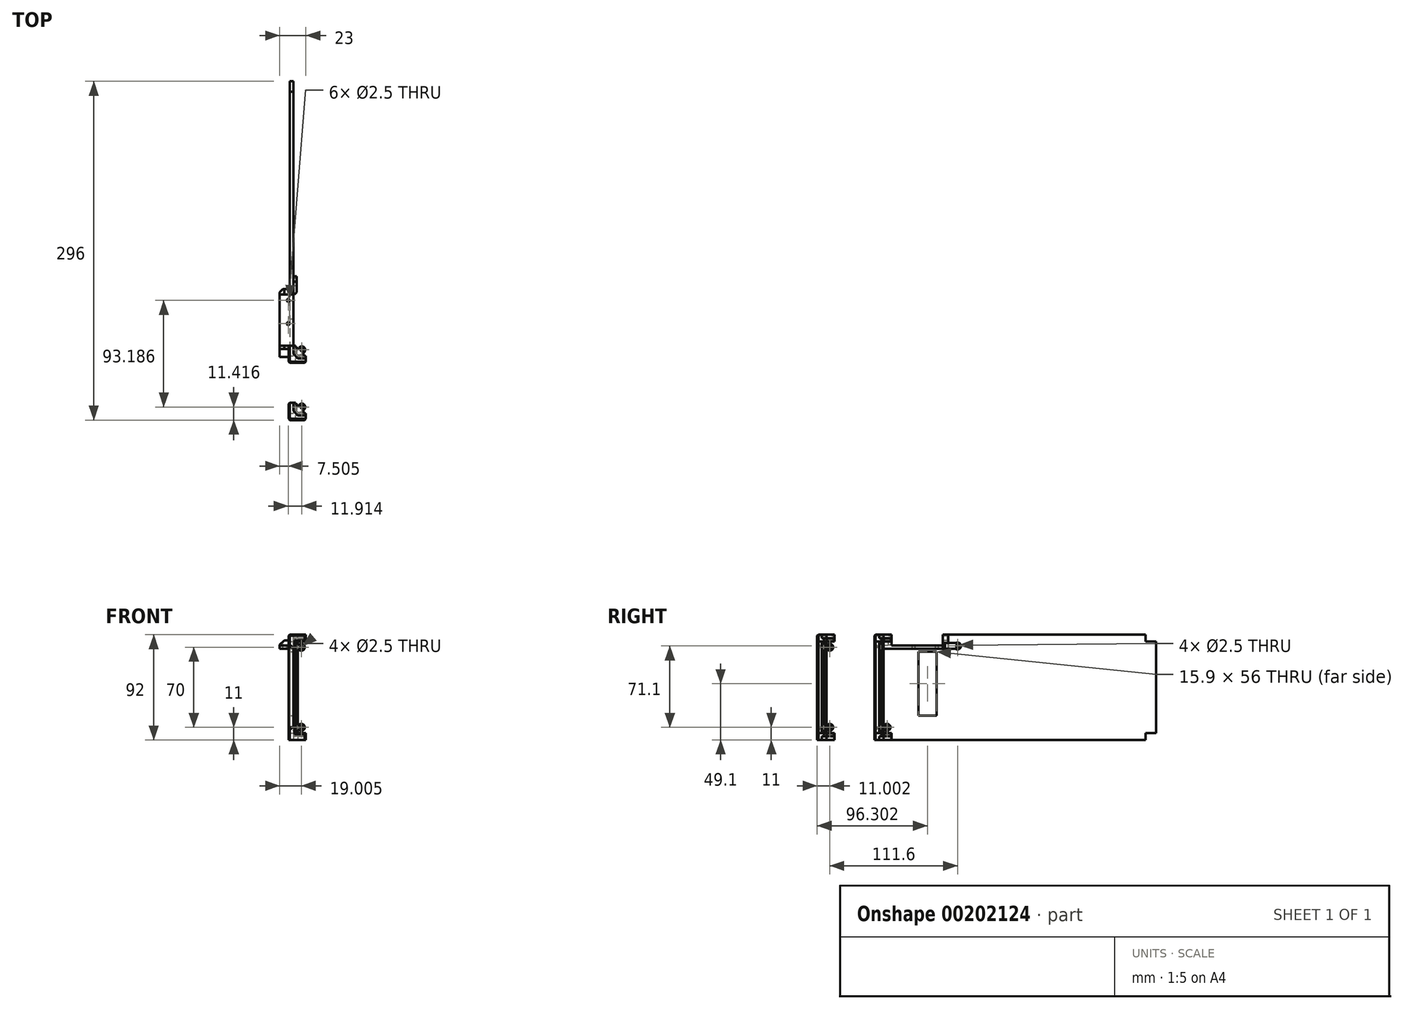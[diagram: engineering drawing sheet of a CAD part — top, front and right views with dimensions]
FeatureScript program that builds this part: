
annotation { "Feature Type Name" : "Feature", "Feature Type Description" : "" }
export const myFeature = defineFeature(function(context is Context, id is Id, definition is map)
    precondition{}
    {
        {
            var Q0;
            Q0=qCreatedBy(makeId("Top.planeOp"),FACE);
            var sketch = newSketch(context, id + "F0", { "sketchPlane" : qUnion([Q0])});
            skLineSegment(sketch, "E0", {"start": v(-30.7, 8.8) * mm, "end": v(-30.7, -6.2) * mm});
            skLineSegment(sketch, "E1", {"start": v(-30.7, -6.2) * mm, "end": v(-15.7, -6.2) * mm});
            skLineSegment(sketch, "E2", {"start": v(-30.7, 8.8) * mm, "end": v(-29.7, 8.8) * mm});
            skLineSegment(sketch, "E3", {"start": v(-15.7, -6.2) * mm, "end": v(-15.7, -5.2) * mm});
            skLineSegment(sketch, "E4", {"start": v(-29.7, 8.8) * mm, "end": v(-24.7, 8.8) * mm});
            skLineSegment(sketch, "E5", {"start": v(-15.7, -5.2) * mm, "end": v(-15.7, -0.2) * mm});
            skLineSegment(sketch, "E6", {"start": v(-24.7, 8.8) * mm, "end": v(-24.7, -0.2) * mm});
            skLineSegment(sketch, "E7", {"start": v(-24.7, -0.2) * mm, "end": v(-15.7, -0.2) * mm});
            skSolve(sketch);
        }
        {
            var Q0;
            Q0=makeQuery(id+"F0.imprint","IMPRINT",FACE,{"disambiguationData":[TD([[makeQuery(id+"F0.imprint","IMPRINT",EDGE,{"derivedFrom":sQuery(id+"F0.wireOp",EDGE,"E0")}),1.0]])]});
            extrude(context, id + "F1", {"entities" : qUnion([Q0]), "depth" : 6 * mm});
        }
        {
            var Q0;
            Q0=makeQuery(id+"F1.opExtrude","CAP_FACE",FACE,{"disambiguationData":[OSD([sQuery(id+"F0.wireOp",EDGE,"E0"),sQuery(id+"F0.wireOp",EDGE,"E1"),sQuery(id+"F0.wireOp",EDGE,"E2"),sQuery(id+"F0.wireOp",EDGE,"E3"),sQuery(id+"F0.wireOp",EDGE,"E4"),sQuery(id+"F0.wireOp",EDGE,"E5"),sQuery(id+"F0.wireOp",EDGE,"E6"),sQuery(id+"F0.wireOp",EDGE,"E7")])],"isStart":false});
            var sketch = newSketch(context, id + "F2", { "sketchPlane" : qUnion([Q0])});
            skLineSegment(sketch, "E8.top", {"start": v(-30.7, -0.2) * mm, "end": v(-24.7, -0.2) * mm});
            skLineSegment(sketch, "E9", {"start": v(-24.7, -0.2) * mm, "end": v(-24.7, 1.8) * mm});
            skLineSegment(sketch, "E10", {"start": v(-24.7, 1.8) * mm, "end": v(-26.7, 1.8) * mm});
            skLineSegment(sketch, "E11", {"start": v(-26.7, 1.8) * mm, "end": v(-26.7, -0.2) * mm});
            skLineSegment(sketch, "E12", {"start": v(-24.7, -0.2) * mm, "end": v(-22.7, -0.2) * mm});
            skLineSegment(sketch, "E13", {"start": v(-22.7, -0.2) * mm, "end": v(-22.7, -2.2) * mm});
            skLineSegment(sketch, "E14", {"start": v(-22.7, -2.2) * mm, "end": v(-24.7, -2.2) * mm});
            skLineSegment(sketch, "E15", {"start": v(-24.7, -6.2) * mm, "end": v(-29.7, -6.2) * mm});
            skLineSegment(sketch, "E16", {"start": v(-24.7, -6.2) * mm, "end": v(-24.7, -2.2) * mm});
            skLineSegment(sketch, "E17", {"start": v(-24.7, -0.2) * mm, "end": v(-24.7, -2.2) * mm});
            skLineSegment(sketch, "E18", {"start": v(-30.7, -0.2) * mm, "end": v(-30.7, -5.2) * mm});
            skLineSegment(sketch, "E19", {"start": v(-30.7, -5.2) * mm, "end": v(-29.7, -6.2) * mm});
            skSolve(sketch);
        }
        {
            var Q0;
            Q0=makeQuery(id+"F2.imprint","IMPRINT",FACE,{"disambiguationData":[TD([[makeQuery(id+"F2.imprint","IMPRINT",EDGE,{"derivedFrom":sQuery(id+"F2.wireOp",EDGE,"E8.bottom")}),1.0]])]});
            var Q1;
            {var subQ0=sQuery(id+"F2.wireOp",EDGE,"E12");Q1=makeQuery(id+"F2.imprint","IMPRINT",FACE,{"disambiguationData":[TD([[makeQuery(id+"F2.imprint","IMPRINT",EDGE,{"derivedFrom":subQ0}),-1.0]])]});}
            var Q2;
            Q2=makeQuery(id+"F2.imprint","IMPRINT",FACE,{"disambiguationData":[TD([[makeQuery(id+"F2.imprint","IMPRINT",EDGE,{"derivedFrom":sQuery(id+"F2.wireOp",EDGE,"E15")}),1.0]])]});
            var Q3;
            {var subQ0=sQuery(id+"F2.wireOp",EDGE,"E9");Q3=makeQuery(id+"F2.imprint","IMPRINT",FACE,{"disambiguationData":[TD([[makeQuery(id+"F2.imprint","IMPRINT",EDGE,{"derivedFrom":subQ0}),-1.0]])]});}
            extrude(context, id + "F3", {"entities" : qUnion([Q0, Q1, Q2, Q3]), "operationType" : NewBodyOperationType.ADD, "depth" : 5 * mm});
        }
        {
            var Q0;
            Q0=makeQuery(id+"F3.opExtrude","CAP_FACE",FACE,{"disambiguationData":[OSD([sQuery(id+"F2.wireOp",EDGE,"E8.bottom"),sQuery(id+"F2.wireOp",EDGE,"E8.top"),sQuery(id+"F2.wireOp",EDGE,"E8.left"),sQuery(id+"F2.wireOp",EDGE,"E8.right"),sQuery(id+"F2.wireOp",EDGE,"E9"),sQuery(id+"F2.wireOp",EDGE,"E10"),sQuery(id+"F2.wireOp",EDGE,"E11"),sQuery(id+"F2.wireOp",EDGE,"E12"),sQuery(id+"F2.wireOp",EDGE,"E13"),sQuery(id+"F2.wireOp",EDGE,"E14")])],"isStart":false});
            var sketch = newSketch(context, id + "F4", { "sketchPlane" : qUnion([Q0])});
            skLineSegment(sketch, "E20", {"start": v(-24.7, -6.2) * mm, "end": v(-26.7, -6.2) * mm});
            skLineSegment(sketch, "E21", {"start": v(-30.7, -0.2) * mm, "end": v(-30.7, -2.2) * mm});
            skLineSegment(sketch, "E22", {"start": v(-26.7, -6.2) * mm, "end": v(-30.7, -2.2) * mm});
            skLineSegment(sketch, "E23", {"start": v(-24.7, -6.2) * mm, "end": v(-24.7, -2.2) * mm});
            skLineSegment(sketch, "E24", {"start": v(-24.7, -2.2) * mm, "end": v(-22.7, -2.2) * mm});
            skLineSegment(sketch, "E25", {"start": v(-22.7, -2.2) * mm, "end": v(-22.7, -0.2) * mm});
            skLineSegment(sketch, "E26", {"start": v(-22.7, -0.2) * mm, "end": v(-24.7, -0.2) * mm});
            skLineSegment(sketch, "E27", {"start": v(-24.7, -0.2) * mm, "end": v(-24.7, 1.8) * mm});
            skLineSegment(sketch, "E28", {"start": v(-24.7, 1.8) * mm, "end": v(-26.7, 1.8) * mm});
            skLineSegment(sketch, "E29", {"start": v(-26.7, 1.8) * mm, "end": v(-26.7, -0.2) * mm});
            skLineSegment(sketch, "E30", {"start": v(-26.7, -0.2) * mm, "end": v(-30.7, -0.2) * mm});
            skSolve(sketch);
        }
        {
            var Q0;
            Q0=makeQuery(id+"F4.imprint","IMPRINT",FACE,{"disambiguationData":[TD([[makeQuery(id+"F4.imprint","IMPRINT",EDGE,{"derivedFrom":sQuery(id+"F4.wireOp",EDGE,"E20")}),1.0]])]});
            extrude(context, id + "F5", {"entities" : qUnion([Q0]), "operationType" : NewBodyOperationType.ADD, "depth" : 35 * mm});
        }
        {
            var Q0;
            Q0=makeQuery(id+"F5.boolean.opBoolean","MERGE",FACE,{"derivedFrom":[makeQuery(id+"F3.opExtrude","SWEPT_FACE",FACE,{"disambiguationData":[OSD([sQuery(id+"F2.wireOp",EDGE,"E14")])]}),makeQuery(id+"F5.opExtrude","SWEPT_FACE",FACE,{"disambiguationData":[OSD([sQuery(id+"FcikvxoAmVT8Sga_1.wireOp",EDGE,"Ugr4Xeua-PaRH-PEAE-46ir-bzMubUFrfAmX")])]})]});
            var sketch = newSketch(context, id + "F6", { "sketchPlane" : qUnion([Q0])});
            skLineSegment(sketch, "E31", {"start": v(-22.7, 6) * mm, "end": v(-22.7, 11) * mm});
            skLineSegment(sketch, "E32", {"start": v(-22.7, 11) * mm, "end": v(-19.7, 11) * mm});
            skCircle(sketch, "E33", {"center": v(-19.7, 11) * mm, "radius": 1.25 * mm});
            skCircle(sketch, "E34", {"center": v(-19.7, 11) * mm, "radius": 3 * mm});
            skLineSegment(sketch, "E35", {"start": v(-22.7, 6) * mm, "end": v(-22.7, 9) * mm});
            skLineSegment(sketch, "E36", {"start": v(-22.7, 9) * mm, "end": v(-21.94, 9) * mm});
            skLineSegment(sketch, "E37", {"start": v(-22.7, 11) * mm, "end": v(-22.7, 13) * mm});
            skLineSegment(sketch, "E38", {"start": v(-22.7, 13) * mm, "end": v(-21.94, 13) * mm});
            skSolve(sketch);
        }
        {
            var Q0;
            Q0=makeQuery(id+"F6.imprint","IMPRINT",FACE,{"disambiguationData":[TD([[makeQuery(id+"F6.imprint","IMPRINT",EDGE,{"derivedFrom":sQuery(id+"F6.wireOp",EDGE,"E33")}),-1.0]])]});
            var Q1;
            {var subQ0=sQuery(id+"F6.wireOp",EDGE,"E37");Q1=makeQuery(id+"F6.imprint","IMPRINT",FACE,{"disambiguationData":[TD([[makeQuery(id+"F6.imprint","IMPRINT",EDGE,{"derivedFrom":subQ0}),1.0]])]});}
            var Q2;
            {var subQ0=sQuery(id+"F6.wireOp",EDGE,"E31");Q2=makeQuery(id+"F6.imprint","IMPRINT",FACE,{"disambiguationData":[TD([[makeQuery(id+"F6.imprint","IMPRINT",EDGE,{"derivedFrom":subQ0}),1.0]])]});}
            extrude(context, id + "F7", {"entities" : qUnion([Q0, Q1, Q2]), "operationType" : NewBodyOperationType.ADD, "oppositeDirection" : true, "depth" : 3 * mm});
        }
        {
            var Q0;
            Q0=makeQuery(id+"F5.boolean.opBoolean","MERGE",FACE,{"derivedFrom":[makeQuery(id+"F3.opExtrude","SWEPT_FACE",FACE,{"disambiguationData":[OSD([sQuery(id+"F2.wireOp",EDGE,"E11")])]}),makeQuery(id+"F5.opExtrude","SWEPT_FACE",FACE,{"disambiguationData":[OSD([sQuery(id+"FcikvxoAmVT8Sga_1.wireOp",EDGE,"rjj8wiBv-6VFg-MGKm-luXr-hqUBBP5AjTz5")])]})]});
            var sketch = newSketch(context, id + "F8", { "sketchPlane" : qUnion([Q0])});
            skLineSegment(sketch, "E39", {"start": v(-1.8, 6) * mm, "end": v(-1.8, 9) * mm});
            skLineSegment(sketch, "E40", {"start": v(-1.8, 9) * mm, "end": v(-1.8, 13) * mm});
            skLineSegment(sketch, "E41", {"start": v(-1.8, 11) * mm, "end": v(-4.8, 11) * mm});
            skCircle(sketch, "E42", {"center": v(-4.8, 11) * mm, "radius": 1.25 * mm});
            skCircle(sketch, "E43", {"center": v(-4.8, 11) * mm, "radius": 3 * mm});
            skLineSegment(sketch, "E44", {"start": v(-1.8, 13) * mm, "end": v(-2.56, 13) * mm});
            skLineSegment(sketch, "E45", {"start": v(-1.8, 9) * mm, "end": v(-2.56, 9) * mm});
            skSolve(sketch);
        }
        {
            var Q0;
            Q0 = qSketchRegion(id + "F8", true);
            extrude(context, id + "F9", {"entities" : qUnion([Q0]), "operationType" : NewBodyOperationType.ADD, "oppositeDirection" : true, "depth" : 3 * mm});
        }
        {
            var Q0;
            Q0=makeQuery(id+"F7.opExtrude","SWEPT_FACE",FACE,{"disambiguationData":[OSD([sQuery(id+"F6.wireOp",EDGE,"E38")])]});
            var sketch = newSketch(context, id + "F10", { "sketchPlane" : qUnion([Q0])});
            skLineSegment(sketch, "E46.0", {"start": v(-23.7, 1.8) * mm, "end": v(-24.7, 1.8) * mm});
            skLineSegment(sketch, "E47", {"start": v(-22.7, 0.8) * mm, "end": v(-23.7, 1.8) * mm});
            skLineSegment(sketch, "E48", {"start": v(-24.7, 1.8) * mm, "end": v(-24.7, -0.2) * mm});
            skLineSegment(sketch, "E49", {"start": v(-24.7, -0.2) * mm, "end": v(-22.7, -0.2) * mm});
            skLineSegment(sketch, "E50", {"start": v(-22.7, -0.2) * mm, "end": v(-22.7, 0.8) * mm});
            skSolve(sketch);
        }
        {
            var Q0;
            Q0=makeQuery(id+"F10.imprint","IMPRINT",FACE,{"disambiguationData":[TD([[makeQuery(id+"F10.imprint","IMPRINT",EDGE,{"derivedFrom":sQuery(id+"F10.wireOp",EDGE,"E46.0")}),1.0]])]});
            extrude(context, id + "F11", {"entities" : qUnion([Q0]), "operationType" : NewBodyOperationType.ADD, "oppositeDirection" : true, "depth" : 4 * mm});
        }
        {
            var Q0;
            Q0=makeQuery(id+"F1.opExtrude","CAP_FACE",FACE,{"disambiguationData":[OSD([sQuery(id+"F0.wireOp",EDGE,"E0"),sQuery(id+"F0.wireOp",EDGE,"E1"),sQuery(id+"F0.wireOp",EDGE,"E2"),sQuery(id+"F0.wireOp",EDGE,"E3"),sQuery(id+"F0.wireOp",EDGE,"E4"),sQuery(id+"F0.wireOp",EDGE,"E5"),sQuery(id+"F0.wireOp",EDGE,"E6"),sQuery(id+"F0.wireOp",EDGE,"E7")])],"isStart":true});
            var sketch = newSketch(context, id + "F12", { "sketchPlane" : qUnion([Q0])});
            skLineSegment(sketch, "E51", {"start": v(-15.7, 0.2) * mm, "end": v(-15.7, 2.2) * mm});
            skLineSegment(sketch, "E52", {"start": v(-15.7, 2.2) * mm, "end": v(-22.7, 2.2) * mm});
            skLineSegment(sketch, "E53", {"start": v(-15.7, 0.2) * mm, "end": v(-24.7, 0.2) * mm});
            skLineSegment(sketch, "E54", {"start": v(-24.7, 0.2) * mm, "end": v(-24.7, -8.8) * mm});
            skLineSegment(sketch, "E55", {"start": v(-24.7, -8.8) * mm, "end": v(-26.7, -8.8) * mm});
            skLineSegment(sketch, "E56", {"start": v(-26.7, -8.8) * mm, "end": v(-26.7, -1.8) * mm});
            skLineSegment(sketch, "E57", {"start": v(-22.7, 2.2) * mm, "end": v(-26.7, -1.8) * mm});
            skSolve(sketch);
        }
        {
            var Q0;
            {var subQ0=sQuery(id+"F12.wireOp",EDGE,"E54");Q0=makeQuery(id+"F12.imprint","IMPRINT",FACE,{"disambiguationData":[TD([[makeQuery(id+"F12.imprint","IMPRINT",EDGE,{"derivedFrom":subQ0}),1.0]])]});}
            var Q1;
            Q1=makeQuery(id+"F12.imprint","IMPRINT",FACE,{"disambiguationData":[TD([[makeQuery(id+"F12.imprint","IMPRINT",EDGE,{"derivedFrom":sQuery(id+"F12.wireOp",EDGE,"E51")}),-1.0]])]});
            extrude(context, id + "F13", {"entities" : qUnion([Q0, Q1]), "operationType" : NewBodyOperationType.REMOVE, "oppositeDirection" : true, "depth" : 3 * mm});
        }
        {
            var Q0;
            Q0=makeQuery(id+"F13.boolean.opBoolean","COPY",FACE,{"derivedFrom":makeQuery(id+"F13.opExtrude","CAP_FACE",FACE,{"disambiguationData":[OSD([sQuery(id+"F12.wireOp",EDGE,"E51"),sQuery(id+"F12.wireOp",EDGE,"E52"),sQuery(id+"F12.wireOp",EDGE,"E53"),sQuery(id+"F12.wireOp",EDGE,"E57")])],"isStart":false})});
            var sketch = newSketch(context, id + "F14", { "sketchPlane" : qUnion([Q0])});
            skLineSegment(sketch, "E58", {"start": v(-24.7, 0.2) * mm, "end": v(-24.7, -7.8) * mm});
            skLineSegment(sketch, "E59", {"start": v(-16.7, 0.2) * mm, "end": v(-24.7, -7.8) * mm});
            skLineSegment(sketch, "E60", {"start": v(-20.7, -3.8) * mm, "end": v(-19.3, -5.2) * mm});
            skCircle(sketch, "E61", {"center": v(-19.3, -5.2) * mm, "radius": 1.25 * mm});
            skCircle(sketch, "E62", {"center": v(-19.3, -5.2) * mm, "radius": 3 * mm});
            skLineSegment(sketch, "E63", {"start": v(-16.7, 0.2) * mm, "end": v(-24.7, 0.2) * mm});
            skSolve(sketch);
        }
        {
            var Q0;
            Q0 = qSketchRegion(id + "F14", true);
            extrude(context, id + "F15", {"entities" : qUnion([Q0]), "operationType" : NewBodyOperationType.ADD, "oppositeDirection" : true, "depth" : 3 * mm});
        }
        {
            var Q0;
            Q0=makeQuery(id+"F1.opExtrude","SWEPT_BODY",BODY,{"disambiguationData":[OSD([sQuery(id+"F0.wireOp",EDGE,"E0"),sQuery(id+"F0.wireOp",EDGE,"E1"),sQuery(id+"F0.wireOp",EDGE,"E2"),sQuery(id+"F0.wireOp",EDGE,"E3"),sQuery(id+"F0.wireOp",EDGE,"E4"),sQuery(id+"F0.wireOp",EDGE,"E5"),sQuery(id+"F0.wireOp",EDGE,"E6"),sQuery(id+"F0.wireOp",EDGE,"E7")])]});
            var Q1;
            Q1=makeQuery(id+"F5.opExtrude","CAP_FACE",FACE,{"disambiguationData":[OSD([sQuery(id+"F4.wireOp",EDGE,"E20"),sQuery(id+"F4.wireOp",EDGE,"E21"),sQuery(id+"F4.wireOp",EDGE,"E22"),sQuery(id+"F4.wireOp",EDGE,"E23"),sQuery(id+"F4.wireOp",EDGE,"E24"),sQuery(id+"F4.wireOp",EDGE,"E25"),sQuery(id+"F4.wireOp",EDGE,"E26"),sQuery(id+"F4.wireOp",EDGE,"E27"),sQuery(id+"F4.wireOp",EDGE,"E28"),sQuery(id+"F4.wireOp",EDGE,"E29"),sQuery(id+"F4.wireOp",EDGE,"E30")])],"isStart":false});
            mirror(context, id + "F16", {"operationType" : NewBodyOperationType.ADD, "entities" : qUnion([Q0]), "mirrorPlane" : qUnion([Q1])});
        }
        {
            var Q0;
            Q0=makeQuery(id+"FhzFfjnD5mDQNPN_1.boolean.opBoolean","MERGE",EDGE,{"derivedFrom":[makeQuery(id+"FrQZREyW5eWcuGQ_1.boolean.opBoolean","MERGE",EDGE,{"derivedFrom":[makeQuery(id+"F1.opExtrude","SWEPT_EDGE",EDGE,{"disambiguationData":[OSD([sQuery(id+"F0.wireOp",EDGE,"E0"),sQuery(id+"F0.wireOp",EDGE,"E1")])]}),makeQuery(id+"FrQZREyW5eWcuGQ_1.opExtrude","SWEPT_EDGE",EDGE,{"disambiguationData":[OSD([sQuery(id+"FOzdUzQN7WSNxo8_1.wireOp",EDGE,"WiYNZVCE-U4Jg-TT48-NUzQ-lxR1TrsUEIwd"),sQuery(id+"FOzdUzQN7WSNxo8_1.wireOp",EDGE,"8d8B1xfc-AYmp-EXSV-HG8z-yugG2Eprzqf7")])]})]}),makeQuery(id+"FhzFfjnD5mDQNPN_1.opExtrude","CAP_EDGE",EDGE,{"disambiguationData":[OSD([sQuery(id+"FUuBHju1a3qaWlO_1.wireOp",EDGE,"Y2hAY4q1-hRi0-7PEO-YUI0-E3ofIxBZuGLo")])],"isStart":true})]});
            var Q1;
            {var subQ0=makeQuery(id+"F5.boolean.opBoolean","MERGE",EDGE,{"derivedFrom":[makeQuery(id+"F3.opExtrude","SWEPT_EDGE",EDGE,{"disambiguationData":[OSD([sQuery(id+"F0.wireOp",EDGE,"E1"),sQuery(id+"F2.wireOp",EDGE,"E15"),sQuery(id+"F2.wireOp",EDGE,"E16")])]}),makeQuery(id+"F5.opExtrude","SWEPT_EDGE",EDGE,{"disambiguationData":[OSD([sQuery(id+"F4.wireOp",EDGE,"E20"),sQuery(id+"F4.wireOp",EDGE,"E23")])]})]});Q1=makeQuery(id+"F16.boolean.opBoolean","MERGE",EDGE,{"derivedFrom":[subQ0,makeQuery(id+"F16.opPattern","COPY",EDGE,{"derivedFrom":subQ0,"instanceName":"1"})]});}
            var Q2;
            {var subQ0=sQuery(id+"F0.wireOp",EDGE,"E1");Q2=makeQuery(id+"F3.boolean.opBoolean","SPLIT",EDGE,{"disambiguationData":[TD([makeQuery(id+"F3.opExtrude","SWEPT_FACE",FACE,{"disambiguationData":[OSD([sQuery(id+"F2.wireOp",EDGE,"E16")])]})])],"derivedFrom":makeQuery(id+"F1.opExtrude","CAP_EDGE",EDGE,{"disambiguationData":[OSD([subQ0])],"isStart":false})});}
            var Q3;
            {var subQ2=sQuery(id+"F0.wireOp",EDGE,"E0");Q3=makeQuery(id+"F3.boolean.opBoolean","SPLIT",EDGE,{"disambiguationData":[TD([makeQuery(id+"F3.opExtrude","SWEPT_FACE",FACE,{"disambiguationData":[OSD([sQuery(id+"F2.wireOp",EDGE,"E8.top")])]})])],"derivedFrom":makeQuery(id+"F1.opExtrude","CAP_EDGE",EDGE,{"disambiguationData":[OSD([subQ2])],"isStart":false})});}
            var Q4;
            {var subQ0=makeQuery(id+"F5.boolean.opBoolean","MERGE",EDGE,{"derivedFrom":[makeQuery(id+"F3.opExtrude","SWEPT_EDGE",EDGE,{"disambiguationData":[OSD([sQuery(id+"F0.wireOp",EDGE,"E0"),sQuery(id+"F2.wireOp",EDGE,"E8.top"),sQuery(id+"F2.wireOp",EDGE,"E18")])]}),makeQuery(id+"F5.opExtrude","SWEPT_EDGE",EDGE,{"disambiguationData":[OSD([sQuery(id+"F4.wireOp",EDGE,"E21"),sQuery(id+"F4.wireOp",EDGE,"E30")])]})]});Q4=makeQuery(id+"F16.boolean.opBoolean","MERGE",EDGE,{"derivedFrom":[subQ0,makeQuery(id+"F16.opPattern","COPY",EDGE,{"derivedFrom":subQ0,"instanceName":"1"})]});}
            var Q5;
            {var subQ2=sQuery(id+"F0.wireOp",EDGE,"E0");Q5=makeQuery(id+"F16.opPattern","COPY",EDGE,{"derivedFrom":makeQuery(id+"F3.boolean.opBoolean","SPLIT",EDGE,{"disambiguationData":[TD([makeQuery(id+"F3.opExtrude","SWEPT_FACE",FACE,{"disambiguationData":[OSD([sQuery(id+"F2.wireOp",EDGE,"E8.top")])]})])],"derivedFrom":makeQuery(id+"F1.opExtrude","CAP_EDGE",EDGE,{"disambiguationData":[OSD([subQ2])],"isStart":false})}),"instanceName":"1"});}
            var Q6;
            {var subQ0=sQuery(id+"F0.wireOp",EDGE,"E1");Q6=makeQuery(id+"F16.opPattern","COPY",EDGE,{"derivedFrom":makeQuery(id+"F3.boolean.opBoolean","SPLIT",EDGE,{"disambiguationData":[TD([makeQuery(id+"F3.opExtrude","SWEPT_FACE",FACE,{"disambiguationData":[OSD([sQuery(id+"F2.wireOp",EDGE,"E16")])]})])],"derivedFrom":makeQuery(id+"F1.opExtrude","CAP_EDGE",EDGE,{"disambiguationData":[OSD([subQ0])],"isStart":false})}),"instanceName":"1"});}
            var Q7;
            Q7=makeQuery(id+"F16.opPattern","COPY",EDGE,{"derivedFrom":makeQuery(id+"F1.opExtrude","SWEPT_EDGE",EDGE,{"disambiguationData":[OSD([sQuery(id+"F0.wireOp",EDGE,"E1"),sQuery(id+"F0.wireOp",EDGE,"E3")])]}),"instanceName":"1"});
            var Q8;
            Q8=makeQuery(id+"F16.opPattern","COPY",EDGE,{"derivedFrom":makeQuery(id+"F1.opExtrude","SWEPT_EDGE",EDGE,{"disambiguationData":[OSD([sQuery(id+"F0.wireOp",EDGE,"E0"),sQuery(id+"F0.wireOp",EDGE,"E2")])]}),"instanceName":"1"});
            var Q9;
            Q9=makeQuery(id+"FrQZREyW5eWcuGQ_1.boolean.opBoolean","MERGE",EDGE,{"derivedFrom":[makeQuery(id+"F1.opExtrude","SWEPT_EDGE",EDGE,{"disambiguationData":[OSD([sQuery(id+"F0.wireOp",EDGE,"E0"),sQuery(id+"F0.wireOp",EDGE,"E2")])]}),makeQuery(id+"FrQZREyW5eWcuGQ_1.opExtrude","SWEPT_EDGE",EDGE,{"disambiguationData":[OSD([sQuery(id+"FOzdUzQN7WSNxo8_1.wireOp",EDGE,"bvd9bl0E-zov9-mno0-jdsr-QOLO0tRtuMB9"),sQuery(id+"FOzdUzQN7WSNxo8_1.wireOp",EDGE,"WiYNZVCE-U4Jg-TT48-NUzQ-lxR1TrsUEIwd")])]})]});
            var Q10;
            Q10=makeQuery(id+"FrQZREyW5eWcuGQ_1.boolean.opBoolean","MERGE",EDGE,{"derivedFrom":[makeQuery(id+"F1.opExtrude","SWEPT_EDGE",EDGE,{"disambiguationData":[OSD([sQuery(id+"F0.wireOp",EDGE,"E1"),sQuery(id+"F0.wireOp",EDGE,"E3")])]}),makeQuery(id+"FrQZREyW5eWcuGQ_1.opExtrude","SWEPT_EDGE",EDGE,{"disambiguationData":[OSD([sQuery(id+"FOzdUzQN7WSNxo8_1.wireOp",EDGE,"8d8B1xfc-AYmp-EXSV-HG8z-yugG2Eprzqf7"),sQuery(id+"FOzdUzQN7WSNxo8_1.wireOp",EDGE,"MSLuVhra-DmRv-DVba-FcVb-sEYbxNxOgFvK")])]})]});
            var Q11;
            Q11=makeQuery(id+"FhzFfjnD5mDQNPN_1.opExtrude","CAP_EDGE",EDGE,{"disambiguationData":[OSD([sQuery(id+"FUuBHju1a3qaWlO_1.wireOp",EDGE,"4F8UiIUv-5H1C-12AU-MrLI-4g8t5kWoGJfL")])],"isStart":true});
            var Q12;
            Q12=makeQuery(id+"FLNWeMOsxUtLRx3_1.boolean.opBoolean","MERGE",EDGE,{"derivedFrom":[makeQuery(id+"FhzFfjnD5mDQNPN_1.opExtrude","SWEPT_EDGE",EDGE,{"disambiguationData":[OSD([sQuery(id+"FUuBHju1a3qaWlO_1.wireOp",EDGE,"Y2hAY4q1-hRi0-7PEO-YUI0-E3ofIxBZuGLo"),sQuery(id+"FUuBHju1a3qaWlO_1.wireOp",EDGE,"4F8UiIUv-5H1C-12AU-MrLI-4g8t5kWoGJfL")])]}),makeQuery(id+"FLNWeMOsxUtLRx3_1.opExtrude","CAP_EDGE",EDGE,{"disambiguationData":[OSD([sQuery(id+"FLM7EheutEo60uB_1.wireOp",EDGE,"BrBLu7pY-tHSo-Owc5-F9vD-osR30emi00rM")])],"isStart":true})]});
            var Q13;
            Q13=makeQuery(id+"F16.opPattern","COPY",EDGE,{"derivedFrom":makeQuery(id+"F1.opExtrude","CAP_EDGE",EDGE,{"disambiguationData":[OSD([sQuery(id+"F0.wireOp",EDGE,"E1")])],"isStart":true}),"instanceName":"1"});
            var Q14;
            Q14=makeQuery(id+"F16.opPattern","COPY",EDGE,{"derivedFrom":makeQuery(id+"F1.opExtrude","SWEPT_EDGE",EDGE,{"disambiguationData":[OSD([sQuery(id+"F0.wireOp",EDGE,"E0"),sQuery(id+"F0.wireOp",EDGE,"E1")])]}),"instanceName":"1"});
            var Q15;
            Q15=makeQuery(id+"F16.opPattern","COPY",EDGE,{"derivedFrom":makeQuery(id+"F1.opExtrude","CAP_EDGE",EDGE,{"disambiguationData":[OSD([sQuery(id+"F0.wireOp",EDGE,"E0")])],"isStart":true}),"instanceName":"1"});
            chamfer(context, id + "F17", {"entities" : qUnion([Q0, Q1, Q2, Q3, Q4, Q5, Q6, Q7, Q8, Q9, Q10, Q11, Q12, Q13, Q14, Q15]), "width" : 1 * mm, "tangentPropagation" : true});
        }
        {
            var Q0;
            Q0=makeQuery(id+"F3.opExtrude","CAP_EDGE",EDGE,{"disambiguationData":[OSD([sQuery(id+"F2.wireOp",EDGE,"E19")])],"isStart":false});
            var Q1;
            Q1=makeQuery(id+"F16.opPattern","COPY",EDGE,{"derivedFrom":makeQuery(id+"F3.opExtrude","CAP_EDGE",EDGE,{"disambiguationData":[OSD([sQuery(id+"F2.wireOp",EDGE,"E19")])],"isStart":false}),"instanceName":"1"});
            chamfer(context, id + "F18", {"entities" : qUnion([Q0, Q1]), "width" : 2 * mm, "tangentPropagation" : true});
        }
        {
            var Q0;
            Q0=makeQuery(id+"F1.opExtrude","SWEPT_BODY",BODY,{"disambiguationData":[OSD([sQuery(id+"F0.wireOp",EDGE,"E0"),sQuery(id+"F0.wireOp",EDGE,"E1"),sQuery(id+"F0.wireOp",EDGE,"E2"),sQuery(id+"F0.wireOp",EDGE,"E3"),sQuery(id+"F0.wireOp",EDGE,"E4"),sQuery(id+"F0.wireOp",EDGE,"E5"),sQuery(id+"F0.wireOp",EDGE,"E6"),sQuery(id+"F0.wireOp",EDGE,"E7")])]});
            transform(context, id + "F19", {"entities" : qUnion([Q0]), "transformType" : TransformType.TRANSLATION_3D, "dx" : 0 * mm, "dy" : 50 * mm, "dz" : 0 * mm, "makeCopy" : true});
        }
        {
            var Q0;
            {var subQ0=makeQuery(id+"F9.boolean.opBoolean","MERGE",FACE,{"derivedFrom":[makeQuery(id+"F5.boolean.opBoolean","MERGE",FACE,{"derivedFrom":[makeQuery(id+"F3.opExtrude","SWEPT_FACE",FACE,{"disambiguationData":[OSD([sQuery(id+"F2.wireOp",EDGE,"E11")])]}),makeQuery(id+"F5.opExtrude","SWEPT_FACE",FACE,{"disambiguationData":[OSD([sQuery(id+"F4.wireOp",EDGE,"E29")])]})]}),makeQuery(id+"F9.opExtrude","CAP_FACE",FACE,{"disambiguationData":[OSD([sQuery(id+"F8.wireOp",EDGE,"E40"),sQuery(id+"F8.wireOp",EDGE,"E42"),sQuery(id+"F8.wireOp",EDGE,"E43"),sQuery(id+"F8.wireOp",EDGE,"E44"),sQuery(id+"F8.wireOp",EDGE,"E45")])],"isStart":true})]});Q0=makeQuery(id+"F19.opPattern","COPY",FACE,{"derivedFrom":makeQuery(id+"F16.boolean.opBoolean","MERGE",FACE,{"derivedFrom":[subQ0,makeQuery(id+"F16.opPattern","COPY",FACE,{"derivedFrom":subQ0,"instanceName":"1"})]}),"instanceName":"1"});}
            var sketch = newSketch(context, id + "F20", { "sketchPlane" : qUnion([Q0])});
            skLineSegment(sketch, "E64.bottom", {"start": v(-51.8, 86) * mm, "end": v(-58.99, 86) * mm});
            skLineSegment(sketch, "E64.top", {"start": v(-51.8, 74.14) * mm, "end": v(-58.99, 74.14) * mm});
            skLineSegment(sketch, "E64.left", {"start": v(-51.8, 86) * mm, "end": v(-51.8, 74.14) * mm});
            skLineSegment(sketch, "E64.right", {"start": v(-58.99, 86) * mm, "end": v(-58.99, 74.14) * mm});
            skSolve(sketch);
        }
        {
            var Q0;
            Q0 = qSketchRegion(id + "F20", true);
            extrude(context, id + "F21", {"entities" : qUnion([Q0]), "operationType" : NewBodyOperationType.REMOVE, "oppositeDirection" : true, "depth" : 25 * mm});
        }
        {
            var Q0;
            {var subQ0=makeQuery(id+"F9.boolean.opBoolean","MERGE",FACE,{"derivedFrom":[makeQuery(id+"F5.boolean.opBoolean","MERGE",FACE,{"derivedFrom":[makeQuery(id+"F3.opExtrude","SWEPT_FACE",FACE,{"disambiguationData":[OSD([sQuery(id+"F2.wireOp",EDGE,"E11")])]}),makeQuery(id+"F5.opExtrude","SWEPT_FACE",FACE,{"disambiguationData":[OSD([sQuery(id+"F4.wireOp",EDGE,"E29")])]})]}),makeQuery(id+"F9.opExtrude","CAP_FACE",FACE,{"disambiguationData":[OSD([sQuery(id+"F8.wireOp",EDGE,"E40"),sQuery(id+"F8.wireOp",EDGE,"E42"),sQuery(id+"F8.wireOp",EDGE,"E43"),sQuery(id+"F8.wireOp",EDGE,"E44"),sQuery(id+"F8.wireOp",EDGE,"E45")])],"isStart":true})]});Q0=makeQuery(id+"F19.opPattern","COPY",FACE,{"derivedFrom":makeQuery(id+"F16.boolean.opBoolean","MERGE",FACE,{"derivedFrom":[subQ0,makeQuery(id+"F16.opPattern","COPY",FACE,{"derivedFrom":subQ0,"instanceName":"1"})]}),"instanceName":"1"});}
            var sketch = newSketch(context, id + "F22", { "sketchPlane" : qUnion([Q0])});
            skLineSegment(sketch, "E65", {"start": v(-51.8, 6) * mm, "end": v(-49.8, 6) * mm});
            skLineSegment(sketch, "E66", {"start": v(-49.8, 6) * mm, "end": v(-49.8, 86) * mm});
            skLineSegment(sketch, "E67", {"start": v(-51.8, 6) * mm, "end": v(-58.8, 6) * mm});
            skLineSegment(sketch, "E68", {"start": v(-58.8, 6) * mm, "end": v(-58.8, 3) * mm});
            skLineSegment(sketch, "E69", {"start": v(-58.8, 3) * mm, "end": v(-88.8, 3) * mm});
            skLineSegment(sketch, "E70", {"start": v(-88.8, 3) * mm, "end": v(-258.8, 3) * mm});
            skLineSegment(sketch, "E71", {"start": v(-88.8, 3) * mm, "end": v(-90.1, 3) * mm});
            skLineSegment(sketch, "E72", {"start": v(-90.1, 3) * mm, "end": v(-90.1, 21.1) * mm});
            skLineSegment(sketch, "E73.bottom", {"start": v(-98.04, 77.1) * mm, "end": v(-82.14, 77.1) * mm});
            skLineSegment(sketch, "E73.top", {"start": v(-98.04, 21.1) * mm, "end": v(-82.14, 21.1) * mm});
            skLineSegment(sketch, "E73.left", {"start": v(-98.04, 77.1) * mm, "end": v(-98.04, 21.1) * mm});
            skLineSegment(sketch, "E73.right", {"start": v(-82.14, 77.1) * mm, "end": v(-82.14, 21.1) * mm});
            skLineSegment(sketch, "E74", {"start": v(-90.1, 21.1) * mm, "end": v(-90.1, 82.6) * mm});
            skLineSegment(sketch, "E75", {"start": v(-82.14, 77.1) * mm, "end": v(-61.84, 77.1) * mm});
            skLineSegment(sketch, "E76.bottom", {"start": v(-61.84, 77.1) * mm, "end": v(-77.74, 77.1) * mm});
            skLineSegment(sketch, "E76.top", {"start": v(-61.84, 21.1) * mm, "end": v(-77.74, 21.1) * mm});
            skLineSegment(sketch, "E76.left", {"start": v(-61.84, 77.1) * mm, "end": v(-61.84, 21.1) * mm});
            skLineSegment(sketch, "E76.right", {"start": v(-77.74, 77.1) * mm, "end": v(-77.74, 21.1) * mm});
            skLineSegment(sketch, "E77", {"start": v(-90.1, 3) * mm, "end": v(-90.1, 13) * mm});
            skLineSegment(sketch, "E78", {"start": v(-90.1, 13) * mm, "end": v(-258.8, 13) * mm});
            skLineSegment(sketch, "E79", {"start": v(-258.8, 13) * mm, "end": v(-258.8, 3) * mm});
            skLineSegment(sketch, "E80", {"start": v(-258.8, 3) * mm, "end": v(-288.8, 3) * mm});
            skSolve(sketch);
        }
        {
            var Q0;
            {var subQ0=makeQuery(id+"F9.boolean.opBoolean","MERGE",FACE,{"derivedFrom":[makeQuery(id+"F5.boolean.opBoolean","MERGE",FACE,{"derivedFrom":[makeQuery(id+"F3.opExtrude","SWEPT_FACE",FACE,{"disambiguationData":[OSD([sQuery(id+"F2.wireOp",EDGE,"E11")])]}),makeQuery(id+"F5.opExtrude","SWEPT_FACE",FACE,{"disambiguationData":[OSD([sQuery(id+"F4.wireOp",EDGE,"E29")])]})]}),makeQuery(id+"F9.opExtrude","CAP_FACE",FACE,{"disambiguationData":[OSD([sQuery(id+"F8.wireOp",EDGE,"E40"),sQuery(id+"F8.wireOp",EDGE,"E42"),sQuery(id+"F8.wireOp",EDGE,"E43"),sQuery(id+"F8.wireOp",EDGE,"E44"),sQuery(id+"F8.wireOp",EDGE,"E45")])],"isStart":true})]});Q0=makeQuery(id+"F19.opPattern","COPY",FACE,{"derivedFrom":makeQuery(id+"F16.boolean.opBoolean","MERGE",FACE,{"derivedFrom":[subQ0,makeQuery(id+"F16.opPattern","COPY",FACE,{"derivedFrom":subQ0,"instanceName":"1"})]}),"instanceName":"1"});}
            var sketch = newSketch(context, id + "F23", { "sketchPlane" : qUnion([Q0])});
            skPoint(sketch, "E81.0", {"position": v(-90.1, 82.6) * mm});
            skPoint(sketch, "E82.0", {"position": v(-88.8, 3) * mm});
            skLineSegment(sketch, "E83", {"start": v(-88.8, 3) * mm, "end": v(-49.8, 3) * mm});
            skLineSegment(sketch, "E84", {"start": v(-49.8, 3) * mm, "end": v(-49.8, 6) * mm});
            skLineSegment(sketch, "E85", {"start": v(-88.8, 3) * mm, "end": v(-98.4, 3) * mm});
            skLineSegment(sketch, "E86", {"start": v(-98.4, 3) * mm, "end": v(-98.4, 82.6) * mm});
            skLineSegment(sketch, "E87", {"start": v(-98.4, 82.6) * mm, "end": v(-78.1, 82.6) * mm});
            skLineSegment(sketch, "E88", {"start": v(-98.4, 82.6) * mm, "end": v(-103.4, 82.6) * mm});
            skPoint(sketch, "E89.0", {"position": v(-58.8, 92) * mm});
            skLineSegment(sketch, "E90", {"start": v(-103.4, 82.6) * mm, "end": v(-103.4, 92) * mm});
            skLineSegment(sketch, "E91", {"start": v(-103.4, 92) * mm, "end": v(-108.4, 92) * mm});
            skLineSegment(sketch, "E92", {"start": v(-103.4, 92) * mm, "end": v(-103.4, 89) * mm});
            skLineSegment(sketch, "E93", {"start": v(-78.1, 82.6) * mm, "end": v(-58.8, 82.6) * mm});
            skLineSegment(sketch, "E94", {"start": v(-49.8, 79.6) * mm, "end": v(-108.4, 79.6) * mm});
            skLineSegment(sketch, "E95", {"start": v(-108.4, 79.6) * mm, "end": v(-108.4, 92) * mm});
            skLineSegment(sketch, "E96", {"start": v(-58.8, 82.6) * mm, "end": v(-58.8, 87.6) * mm});
            skLineSegment(sketch, "E97", {"start": v(-58.8, 82.6) * mm, "end": v(-48.8, 82.6) * mm});
            skLineSegment(sketch, "E98", {"start": v(-48.8, 82.6) * mm, "end": v(-48.8, 79.6) * mm});
            skLineSegment(sketch, "E99", {"start": v(-48.8, 79.6) * mm, "end": v(-49.8, 79.6) * mm});
            skLineSegment(sketch, "E100", {"start": v(-48.8, 79.6) * mm, "end": v(-48.8, 82.6) * mm});
            skLineSegment(sketch, "E101", {"start": v(-58.8, 87.6) * mm, "end": v(-48.8, 87.6) * mm});
            skLineSegment(sketch, "E102", {"start": v(-48.8, 87.6) * mm, "end": v(-48.8, 82.6) * mm});
            skSolve(sketch);
        }
        {
            var Q0;
            Q0 = qSketchRegion(id + "F23", true);
            extrude(context, id + "F24", {"entities" : qUnion([Q0]), "operationType" : NewBodyOperationType.ADD, "depth" : 4 * mm});
        }
        {
            var Q0;
            Q0=makeQuery(id+"F24.opExtrude","CAP_FACE",FACE,{"disambiguationData":[OSD([sQuery(id+"F23.wireOp",EDGE,"E87"),sQuery(id+"F23.wireOp",EDGE,"E88"),sQuery(id+"F23.wireOp",EDGE,"E90"),sQuery(id+"F23.wireOp",EDGE,"E91"),sQuery(id+"F23.wireOp",EDGE,"E92"),sQuery(id+"F23.wireOp",EDGE,"E93"),sQuery(id+"F23.wireOp",EDGE,"emW7s7Yi-K1XR-Uk5J-ywYN-QYW2KehoLczj"),sQuery(id+"F23.wireOp",EDGE,"E94"),sQuery(id+"F23.wireOp",EDGE,"E95"),sQuery(id+"F23.wireOp",EDGE,"smOKM8jk-HrRC-bj5b-DVTA-jqHB6Uq8j4P8"),sQuery(id+"F23.wireOp",EDGE,"irCT5wbj-C8NX-Zg2D-7k4y-BdeexUpFStGA"),sQuery(id+"F23.wireOp",EDGE,"yi7GR8WY-sdnb-1Ich-WMD9-NlS52SZ6jMQB")])],"isStart":false});
            var sketch = newSketch(context, id + "F25", { "sketchPlane" : qUnion([Q0])});
            skLineSegment(sketch, "E103", {"start": v(-103.4, 82.6) * mm, "end": v(-108.4, 82.6) * mm});
            skLineSegment(sketch, "E104", {"start": v(-108.4, 82.6) * mm, "end": v(-108.4, 79.6) * mm});
            skLineSegment(sketch, "E105", {"start": v(-58.8, 82.6) * mm, "end": v(-55.8, 82.6) * mm});
            skLineSegment(sketch, "E106", {"start": v(-55.8, 82.6) * mm, "end": v(-55.8, 79.6) * mm});
            skLineSegment(sketch, "E107", {"start": v(-55.8, 79.6) * mm, "end": v(-108.4, 79.6) * mm});
            skLineSegment(sketch, "E108", {"start": v(-103.4, 82.6) * mm, "end": v(-58.8, 82.6) * mm});
            skLineSegment(sketch, "E109", {"start": v(-55.8, 82.6) * mm, "end": v(-55.8, 87.1) * mm});
            skLineSegment(sketch, "E110", {"start": v(-55.8, 87.1) * mm, "end": v(-58.8, 87.1) * mm});
            skLineSegment(sketch, "E111", {"start": v(-58.8, 87.1) * mm, "end": v(-58.8, 82.6) * mm});
            skLineSegment(sketch, "E112", {"start": v(-103.4, 82.6) * mm, "end": v(-103.4, 87.1) * mm});
            skLineSegment(sketch, "E113", {"start": v(-103.4, 87.1) * mm, "end": v(-108.4, 87.1) * mm});
            skLineSegment(sketch, "E114", {"start": v(-108.4, 87.1) * mm, "end": v(-108.4, 82.6) * mm});
            skLineSegment(sketch, "E115.0", {"start": v(-48.8, 82.6) * mm, "end": v(-48.8, 5) * mm});
            skLineSegment(sketch, "E116", {"start": v(-55.8, 82.6) * mm, "end": v(-48.8, 82.6) * mm});
            skLineSegment(sketch, "E117", {"start": v(-48.8, 82.6) * mm, "end": v(-48.8, 79.6) * mm});
            skLineSegment(sketch, "E118", {"start": v(-48.8, 79.6) * mm, "end": v(-55.8, 79.6) * mm});
            skSolve(sketch);
        }
        {
            var Q0;
            Q0=makeQuery(id+"F25.imprint","IMPRINT",FACE,{"disambiguationData":[TD([[makeQuery(id+"F25.imprint","IMPRINT",EDGE,{"derivedFrom":sQuery(id+"F25.wireOp",EDGE,"E103")}),-1.0]])]});
            var Q1;
            Q1=makeQuery(id+"F25.imprint","IMPRINT",FACE,{"disambiguationData":[TD([[makeQuery(id+"F25.imprint","IMPRINT",EDGE,{"derivedFrom":sQuery(id+"F25.wireOp",EDGE,"E103")}),1.0]])]});
            var Q2;
            {var subQ0=sQuery(id+"F25.wireOp",EDGE,"E105");Q2=makeQuery(id+"F25.imprint","IMPRINT",FACE,{"disambiguationData":[TD([[makeQuery(id+"F25.imprint","IMPRINT",EDGE,{"derivedFrom":subQ0}),1.0]])]});}
            var Q3;
            {var subQ0=sQuery(id+"F25.wireOp",EDGE,"E106");Q3=makeQuery(id+"F25.imprint","IMPRINT",FACE,{"disambiguationData":[TD([[makeQuery(id+"F25.imprint","IMPRINT",EDGE,{"derivedFrom":subQ0}),1.0]])]});}
            extrude(context, id + "F26", {"entities" : qUnion([Q0, Q1, Q2, Q3]), "operationType" : NewBodyOperationType.ADD, "depth" : 8 * mm});
        }
        {
            var Q0;
            Q0=makeQuery(id+"F26.opExtrude","CAP_EDGE",EDGE,{"disambiguationData":[OSD([sQuery(id+"F25.wireOp",EDGE,"E117")])],"isStart":false});
            var Q1;
            Q1=makeQuery(id+"F26.opExtrude","CAP_EDGE",EDGE,{"disambiguationData":[OSD([sQuery(id+"F25.wireOp",EDGE,"E110")])],"isStart":false});
            var Q2;
            Q2=makeQuery(id+"F26.opExtrude","CAP_EDGE",EDGE,{"disambiguationData":[OSD([sQuery(id+"F25.wireOp",EDGE,"E113")])],"isStart":false});
            chamfer(context, id + "F27", {"entities" : qUnion([Q0, Q1, Q2]), "width" : 4 * mm, "tangentPropagation" : true});
        }
        {
            var Q0;
            Q0=makeQuery(id+"F26.opExtrude","CAP_EDGE",EDGE,{"disambiguationData":[OSD([sQuery(id+"F25.wireOp",EDGE,"E104"),sQuery(id+"F25.wireOp",EDGE,"E114")])],"isStart":false});
            chamfer(context, id + "F28", {"entities" : qUnion([Q0]), "width" : 3 * mm, "tangentPropagation" : true});
        }
        {
            var Q0;
            Q0=makeQuery(id+"F26.boolean.opBoolean","MERGE",FACE,{"derivedFrom":[makeQuery(id+"F24.opExtrude","SWEPT_FACE",FACE,{"disambiguationData":[OSD([sQuery(id+"F23.wireOp",EDGE,"E87"),sQuery(id+"F23.wireOp",EDGE,"E88"),sQuery(id+"F23.wireOp",EDGE,"E93")])]}),makeQuery(id+"F26.opExtrude","SWEPT_FACE",FACE,{"disambiguationData":[OSD([sQuery(id+"F25.wireOp",EDGE,"E108")])]})]});
            var sketch = newSketch(context, id + "F29", { "sketchPlane" : qUnion([Q0])});
            skPoint(sketch, "E119.0", {"position": v(-26.7, 98.4) * mm});
            skLineSegment(sketch, "E120", {"start": v(-26.7, 98.4) * mm, "end": v(-31.2, 98.4) * mm});
            skCircle(sketch, "E121", {"center": v(-31.2, 98.4) * mm, "radius": 1.25 * mm});
            skLineSegment(sketch, "E122", {"start": v(-26.7, 98.4) * mm, "end": v(-26.7, 78.1) * mm});
            skLineSegment(sketch, "E123", {"start": v(-26.7, 78.1) * mm, "end": v(-31.2, 78.1) * mm});
            skCircle(sketch, "E124", {"center": v(-31.2, 78.1) * mm, "radius": 1.25 * mm});
            skSolve(sketch);
        }
        {
            var Q0;
            Q0=makeQuery(id+"F29.imprint","IMPRINT",FACE,{"disambiguationData":[TD([[makeQuery(id+"F29.imprint","IMPRINT",EDGE,{"derivedFrom":sQuery(id+"F29.wireOp",EDGE,"E121")}),1.0]])]});
            var Q1;
            Q1=makeQuery(id+"F29.imprint","IMPRINT",FACE,{"disambiguationData":[TD([[makeQuery(id+"F29.imprint","IMPRINT",EDGE,{"derivedFrom":sQuery(id+"F29.wireOp",EDGE,"E124")}),1.0]])]});
            extrude(context, id + "F30", {"entities" : qUnion([Q0, Q1]), "operationType" : NewBodyOperationType.REMOVE, "oppositeDirection" : true, "depth" : 3 * mm});
        }
        {
            var Q0;
            Q0=makeQuery(id+"F24.opExtrude","CAP_FACE",FACE,{"disambiguationData":[OSD([sQuery(id+"F23.wireOp",EDGE,"E87"),sQuery(id+"F23.wireOp",EDGE,"E88"),sQuery(id+"F23.wireOp",EDGE,"E90"),sQuery(id+"F23.wireOp",EDGE,"E91"),sQuery(id+"F23.wireOp",EDGE,"E92"),sQuery(id+"F23.wireOp",EDGE,"E93"),sQuery(id+"F23.wireOp",EDGE,"emW7s7Yi-K1XR-Uk5J-ywYN-QYW2KehoLczj"),sQuery(id+"F23.wireOp",EDGE,"E94"),sQuery(id+"F23.wireOp",EDGE,"E95"),sQuery(id+"F23.wireOp",EDGE,"smOKM8jk-HrRC-bj5b-DVTA-jqHB6Uq8j4P8"),sQuery(id+"F23.wireOp",EDGE,"irCT5wbj-C8NX-Zg2D-7k4y-BdeexUpFStGA"),sQuery(id+"F23.wireOp",EDGE,"yi7GR8WY-sdnb-1Ich-WMD9-NlS52SZ6jMQB")])],"isStart":true});
            var sketch = newSketch(context, id + "F31", { "sketchPlane" : qUnion([Q0])});
            skLineSegment(sketch, "E125", {"start": v(108.4, 79.6) * mm, "end": v(113.4, 79.6) * mm});
            skLineSegment(sketch, "E126", {"start": v(108.4, 79.6) * mm, "end": v(108.4, 84.6) * mm});
            skLineSegment(sketch, "E127", {"start": v(108.4, 84.6) * mm, "end": v(113.4, 84.6) * mm});
            skLineSegment(sketch, "E128", {"start": v(113.4, 84.6) * mm, "end": v(113.4, 79.6) * mm});
            skLineSegment(sketch, "E129", {"start": v(113.4, 82.1) * mm, "end": v(116.4, 82.1) * mm});
            skCircle(sketch, "E130", {"center": v(116.4, 82.1) * mm, "radius": 1.25 * mm});
            skLineSegment(sketch, "E131", {"start": v(108.4, 84.6) * mm, "end": v(103.4, 84.6) * mm});
            skLineSegment(sketch, "E132", {"start": v(103.4, 84.6) * mm, "end": v(103.4, 79.6) * mm});
            skLineSegment(sketch, "E133", {"start": v(103.4, 79.6) * mm, "end": v(108.4, 79.6) * mm});
            skCircle(sketch, "E134", {"center": v(116.4, 82.1) * mm, "radius": 3 * mm});
            skLineSegment(sketch, "E135", {"start": v(113.4, 79.6) * mm, "end": v(114.73, 79.6) * mm});
            skLineSegment(sketch, "E136", {"start": v(113.4, 84.6) * mm, "end": v(114.73, 84.6) * mm});
            skSolve(sketch);
        }
        {
            var Q0;
            Q0 = qSketchRegion(id + "F31", true);
            extrude(context, id + "F32", {"entities" : qUnion([Q0]), "operationType" : NewBodyOperationType.ADD, "depth" : 3 * mm});
        }
        {
            var Q0;
            Q0=makeQuery(id+"F32.opExtrude","CAP_EDGE",EDGE,{"disambiguationData":[OSD([sQuery(id+"F31.wireOp",EDGE,"E132")])],"isStart":false});
            chamfer(context, id + "F33", {"entities" : qUnion([Q0]), "width" : 2 * mm, "tangentPropagation" : true});
        }
        {
            var Q0;
            Q0=makeQuery(id+"F24.opExtrude","CAP_EDGE",EDGE,{"disambiguationData":[OSD([sQuery(id+"F23.wireOp",EDGE,"E96")])],"isStart":false});
            var Q1;
            Q1=makeQuery(id+"F24.opExtrude","CAP_EDGE",EDGE,{"disambiguationData":[OSD([sQuery(id+"F23.wireOp",EDGE,"E91")])],"isStart":false});
            var Q2;
            Q2=makeQuery(id+"F24.opExtrude","CAP_EDGE",EDGE,{"disambiguationData":[OSD([sQuery(id+"F23.wireOp",EDGE,"E95")])],"isStart":false});
            chamfer(context, id + "F34", {"entities" : qUnion([Q0, Q1, Q2]), "width" : 1 * mm, "tangentPropagation" : true});
        }
        {
            var Q0;
            {var subQ0=makeQuery(id+"F9.boolean.opBoolean","MERGE",FACE,{"derivedFrom":[makeQuery(id+"F5.boolean.opBoolean","MERGE",FACE,{"derivedFrom":[makeQuery(id+"F3.opExtrude","SWEPT_FACE",FACE,{"disambiguationData":[OSD([sQuery(id+"F2.wireOp",EDGE,"E11")])]}),makeQuery(id+"F5.opExtrude","SWEPT_FACE",FACE,{"disambiguationData":[OSD([sQuery(id+"F4.wireOp",EDGE,"E29")])]})]}),makeQuery(id+"F9.opExtrude","CAP_FACE",FACE,{"disambiguationData":[OSD([sQuery(id+"F8.wireOp",EDGE,"E40"),sQuery(id+"F8.wireOp",EDGE,"E42"),sQuery(id+"F8.wireOp",EDGE,"E43"),sQuery(id+"F8.wireOp",EDGE,"E44"),sQuery(id+"F8.wireOp",EDGE,"E45")])],"isStart":true})]});Q0=makeQuery(id+"F19.opPattern","COPY",FACE,{"derivedFrom":makeQuery(id+"F16.boolean.opBoolean","MERGE",FACE,{"derivedFrom":[subQ0,makeQuery(id+"F16.opPattern","COPY",FACE,{"derivedFrom":subQ0,"instanceName":"1"})]}),"instanceName":"1"});}
            var sketch = newSketch(context, id + "F35", { "sketchPlane" : qUnion([Q0])});
            skLineSegment(sketch, "E137", {"start": v(-49.8, 6) * mm, "end": v(-58.8, 6) * mm});
            skLineSegment(sketch, "E138", {"start": v(-58.8, 6) * mm, "end": v(-58.8, 0) * mm});
            skLineSegment(sketch, "E139", {"start": v(-58.8, 0) * mm, "end": v(-280.8, 0) * mm});
            skLineSegment(sketch, "E140", {"start": v(-280.8, 92) * mm, "end": v(-280.8, 86) * mm});
            skLineSegment(sketch, "E141", {"start": v(-280.8, 86) * mm, "end": v(-289.8, 86) * mm});
            skLineSegment(sketch, "E142", {"start": v(-289.8, 86) * mm, "end": v(-289.8, 6) * mm});
            skLineSegment(sketch, "E143", {"start": v(-289.8, 6) * mm, "end": v(-280.8, 6) * mm});
            skLineSegment(sketch, "E144", {"start": v(-280.8, 6) * mm, "end": v(-280.8, 0) * mm});
            skPoint(sketch, "E145.0", {"position": v(-108.4, 92) * mm});
            skLineSegment(sketch, "E146", {"start": v(-108.4, 92) * mm, "end": v(-280.8, 92) * mm});
            skPoint(sketch, "E147.0", {"position": v(-108.4, 79.6) * mm});
            skLineSegment(sketch, "E148", {"start": v(-108.4, 92) * mm, "end": v(-108.4, 79.6) * mm});
            skLineSegment(sketch, "E149", {"start": v(-108.4, 79.6) * mm, "end": v(-49.8, 79.6) * mm});
            skLineSegment(sketch, "E150", {"start": v(-49.8, 79.6) * mm, "end": v(-49.8, 6) * mm});
            skSolve(sketch);
        }
        {
            var Q0;
            Q0 = qSketchRegion(id + "F35", true);
            extrude(context, id + "F36", {"entities" : qUnion([Q0]), "depth" : 3 * mm});
        }
        {
            var Q0;
            {var subQ0=sQuery(id+"F22.wireOp",EDGE,"E73.right");Q0=makeQuery(id+"F22.imprint","IMPRINT",FACE,{"disambiguationData":[TD([[makeQuery(id+"F22.imprint","IMPRINT",EDGE,{"derivedFrom":subQ0}),-1.0]])]});}
            var Q1;
            {var subQ0=sQuery(id+"F22.wireOp",EDGE,"E73.left");Q1=makeQuery(id+"F22.imprint","IMPRINT",FACE,{"disambiguationData":[TD([[makeQuery(id+"F22.imprint","IMPRINT",EDGE,{"derivedFrom":subQ0}),1.0]])]});}
            var Q2;
            Q2=makeQuery(id+"F22.imprint","IMPRINT",FACE,{"disambiguationData":[TD([[makeQuery(id+"F22.imprint","IMPRINT",EDGE,{"derivedFrom":sQuery(id+"F22.wireOp",EDGE,"E76.bottom")}),1.0]])]});
            extrude(context, id + "F37", {"entities" : qUnion([Q0, Q1, Q2]), "operationType" : NewBodyOperationType.REMOVE, "depth" : 25 * mm});
        }
    });
